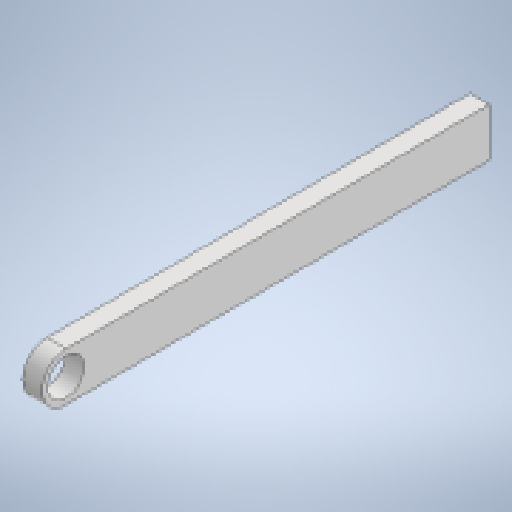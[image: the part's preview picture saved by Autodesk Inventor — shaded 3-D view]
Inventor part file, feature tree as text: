
AUTODESK INVENTOR PART (.ipt)
format: ipt  version: 2023 (Build 270158000, 158)  size: 236,544 bytes
history: native  units: mm
features: extrude x2, sketch x2, other x1, projected_geometry x1
ambient origin geometry x8: Origin, YZ Plane, XZ Plane, XY Plane, X Axis, Y Axis, Z Axis, Center Point
bodies: Body1 (feature_tree)
feature tree (6):
  other  "Bryła1"
  extrude  "Wyciągnięcie proste1"  Depth=3.8mm
  extrude  "Wyciągnięcie proste2"  Depth=5.0mm
  sketch  "Szkic1"
  sketch  "Szkic2"
  projected_geometry  "Pętla rzutowana1"
